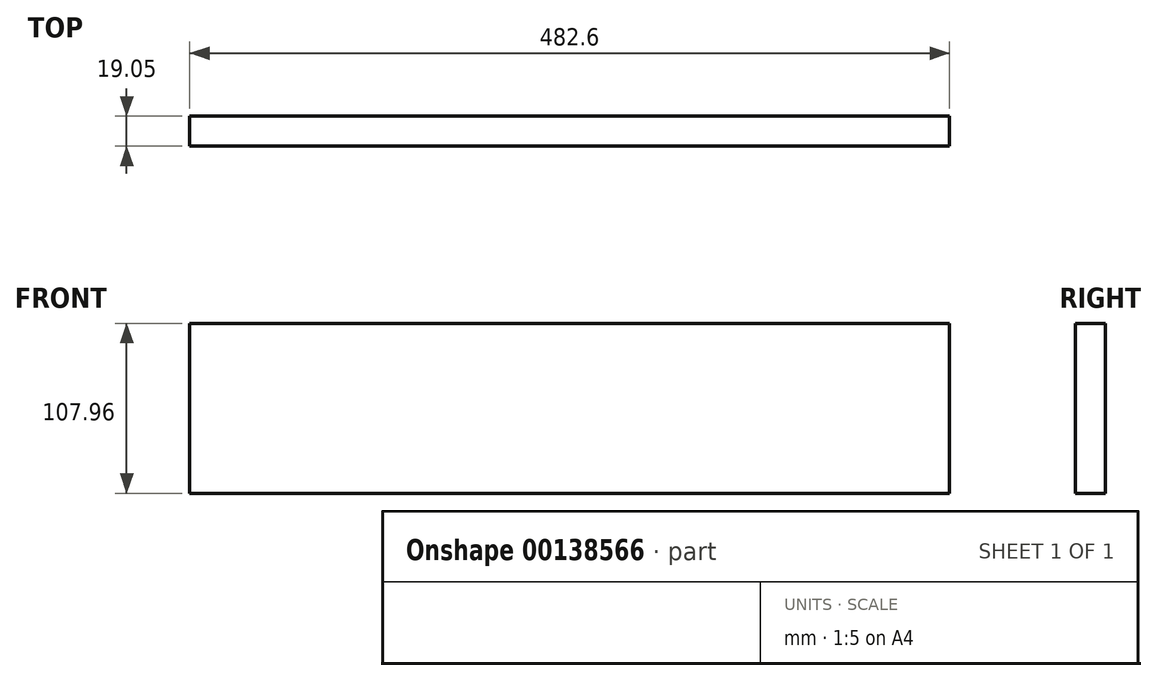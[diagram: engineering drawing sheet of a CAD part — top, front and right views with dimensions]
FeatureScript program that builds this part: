
annotation { "Feature Type Name" : "Feature", "Feature Type Description" : "" }
export const myFeature = defineFeature(function(context is Context, id is Id, definition is map)
    precondition{}
    {
        {
            var Q0;
            Q0=qCreatedBy(makeId("Front.planeOp"),FACE);
            var sketch = newSketch(context, id + "F0", { "sketchPlane" : qUnion([Q0])});
            skLineSegment(sketch, "E0.bottom", {"start": v(-241.3, 53.97) * mm, "end": v(241.3, 53.97) * mm});
            skLineSegment(sketch, "E0.top", {"start": v(-241.3, -53.97) * mm, "end": v(241.3, -53.97) * mm});
            skLineSegment(sketch, "E0.left", {"start": v(-241.3, 53.97) * mm, "end": v(-241.3, -53.97) * mm});
            skLineSegment(sketch, "E0.right", {"start": v(241.3, 53.97) * mm, "end": v(241.3, -53.97) * mm});
            skPoint(sketch, "E0.middle", {"position": v(0, 0) * mm});
            skSolve(sketch);
        }
        {
            var Q0;
            Q0=makeQuery(id+"F0.imprint","IMPRINT",FACE,{"disambiguationData":[TD([[makeQuery(id+"F0.imprint","IMPRINT",EDGE,{"derivedFrom":sQuery(id+"F0.wireOp",EDGE,"E0.bottom")}),-1.0]])]});
            extrude(context, id + "F1", {"entities" : qUnion([Q0]), "depth" : 19.05 * mm});
        }
    });
